# Revit family: Bath-Freestanding-KOHLER-BIOVE-K-8223T_1
name_source: partatom
category: Plumbing Fixtures
revit_build: Autodesk Revit 2017 (Build: 20160225_1515(x64)
units: mm (PartAtom-declared; Revit-internal decimal feet)

## family parameters
Cut with Voids When Loaded = No
Host = Face
OmniClass Number = 23.31.15.00
OmniClass Title = Bathtubs
Part Type = Normal
Room Calculation Point = No
Round Connector Dimension = Use Diameter
Shared = No

## types (2) — shared parameters
ADA Compliant = No
Assembly Code = D2010500
CW Connection = No
Cold Water Inlet = Cold Water Inlet
Date Modified = 01/27/2021
Default Elevation = 0"
Drain Included = Yes
Finish = KOHLER-Cast_Iron-0-White
HW Connection = No
Height = 18 5/16"
Hot Water Inlet = Hot Water Inlet
Length = 29 1/2"
Manufacturer = KOHLER Co.
Master Format 2014 = 22 41 19
Master Format 2014 Name = Residential Bathtubs
Material = Cast Iron
Product Documentation Link = https://files.kohler.com.cn
Product Name = BIOVE
Product Page URL = https://www.kohler.com.cn
URL = http://www.kohler.com.cn
Vent Connection = No
Waste Connection = Yes
Waste Water Outlet = Waste Water Outlet
WaterSense Certified = No
Width = 59 1/16"

## per-type parameters (varying)
| type | Description | GR | Model | Type |
| 0-White | 1.5M CI BATH | No | K-8223T-0 | 1 |
| With Grip Hole, 0-White | 1.5M CI BATH WITH GRIP HOLE | Yes | K-8223T-GR-0 | 2 |

## geometry (parser evidence)
native form markers: Sweep x4
no freeform markers — native parametric forms only
